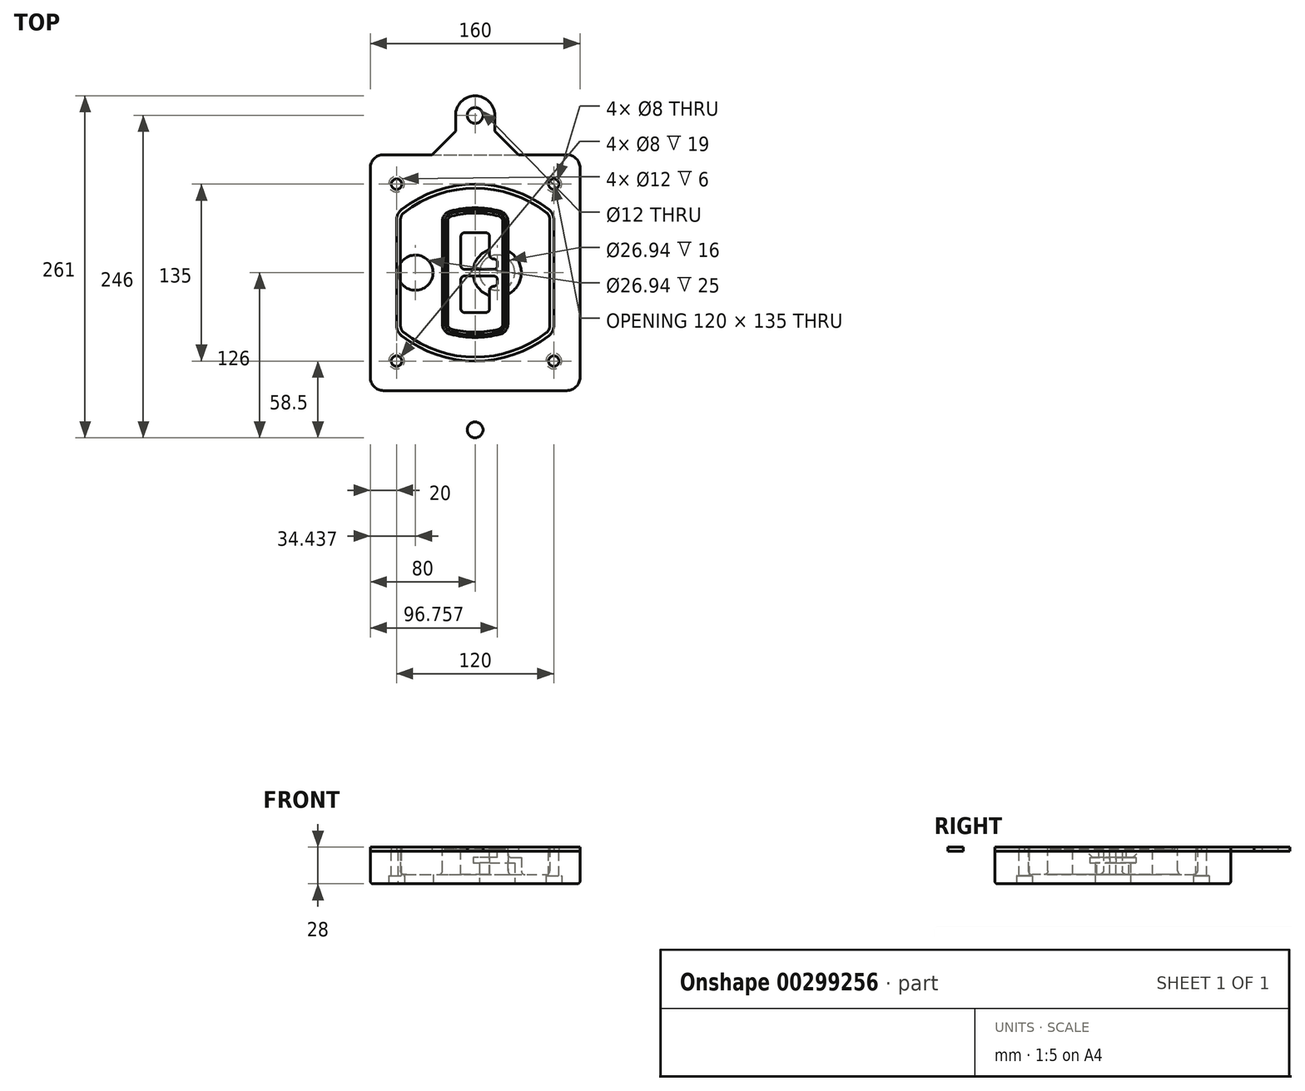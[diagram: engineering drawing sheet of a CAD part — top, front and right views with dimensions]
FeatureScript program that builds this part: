
annotation { "Feature Type Name" : "Feature", "Feature Type Description" : "" }
export const myFeature = defineFeature(function(context is Context, id is Id, definition is map)
    precondition{}
    {
        {
            var Q0;
            Q0=qCreatedBy(makeId("Top.planeOp"),FACE);
            var sketch = newSketch(context, id + "F0", { "sketchPlane" : qUnion([Q0])});
            skPoint(sketch, "E0.rect.middle", {"position": v(0, 0) * mm});
            skLineSegment(sketch, "E1.bottom", {"start": v(-70, -90) * mm, "end": v(70, -90) * mm});
            skLineSegment(sketch, "E1.top", {"start": v(-70, 90) * mm, "end": v(70, 90) * mm});
            skLineSegment(sketch, "E1.left", {"start": v(-80, -80) * mm, "end": v(-80, 80) * mm});
            skLineSegment(sketch, "E1.right", {"start": v(80, -80) * mm, "end": v(80, 80) * mm});
            skLineSegment(sketch, "E2", {"start": v(-80, 90) * mm, "end": v(80, -90) * mm, "construction": true});
            skLineSegment(sketch, "E3", {"start": v(80, 90) * mm, "end": v(-80, -90) * mm, "construction": true});
            skCircle(sketch, "E4", {"center": v(-60, 67.5) * mm, "radius": 4 * mm});
            skCircle(sketch, "E5", {"center": v(60, 67.5) * mm, "radius": 4 * mm});
            skCircle(sketch, "E6", {"center": v(60, -67.5) * mm, "radius": 4 * mm});
            skCircle(sketch, "E7", {"center": v(-60, -67.5) * mm, "radius": 4 * mm});
            skLineSegment(sketch, "E8", {"start": v(-60, 67.5) * mm, "end": v(60, 67.5) * mm, "construction": true});
            skLineSegment(sketch, "E9", {"start": v(60, 67.5) * mm, "end": v(60, -67.5) * mm, "construction": true});
            skLineSegment(sketch, "E10", {"start": v(60, -67.5) * mm, "end": v(-60, -67.5) * mm, "construction": true});
            skLineSegment(sketch, "E11", {"start": v(-60, -67.5) * mm, "end": v(-60, 67.5) * mm, "construction": true});
            skLineSegment(sketch, "E12", {"start": v(-60, 40.3) * mm, "end": v(-60, -40.3) * mm});
            skLineSegment(sketch, "E13", {"start": v(60, 40.3) * mm, "end": v(60, -40.3) * mm});
            skArc(sketch, "E14", {"start": v(56.15, 48.18) * mm, "mid": v(0, 67.5) * mm, "end": v(-56.15, 48.18) * mm});
            skArc(sketch, "E15", {"start": v(-56.15, -48.18) * mm, "mid": v(0, -67.5) * mm, "end": v(56.15, -48.18) * mm});
            skLineSegment(sketch, "E16", {"start": v(-60, 0) * mm, "end": v(60, 0) * mm, "construction": true});
            skPoint(sketch, "E17.visualSharp", {"position": v(-60, -45) * mm});
            skArc(sketch, "E17.filletArc", {"start": v(-60, -40.3) * mm, "mid": v(-58.99, -44.68) * mm, "end": v(-56.15, -48.18) * mm});
            skPoint(sketch, "E18.visualSharp", {"position": v(-60, 45) * mm});
            skArc(sketch, "E18.filletArc", {"start": v(-56.15, 48.18) * mm, "mid": v(-58.99, 44.68) * mm, "end": v(-60, 40.3) * mm});
            skPoint(sketch, "E19.visualSharp", {"position": v(60, 45) * mm});
            skArc(sketch, "E19.filletArc", {"start": v(60, 40.3) * mm, "mid": v(58.99, 44.68) * mm, "end": v(56.15, 48.18) * mm});
            skPoint(sketch, "E20.visualSharp", {"position": v(60, -45) * mm});
            skArc(sketch, "E20.filletArc", {"start": v(56.15, -48.18) * mm, "mid": v(58.99, -44.68) * mm, "end": v(60, -40.3) * mm});
            skPoint(sketch, "E21.visualSharp", {"position": v(-80, 90) * mm});
            skArc(sketch, "E21.filletArc", {"start": v(-70, 90) * mm, "mid": v(-77.07, 87.07) * mm, "end": v(-80, 80) * mm});
            skPoint(sketch, "E22.visualSharp", {"position": v(80, 90) * mm});
            skArc(sketch, "E22.filletArc", {"start": v(80, 80) * mm, "mid": v(77.07, 87.07) * mm, "end": v(70, 90) * mm});
            skPoint(sketch, "E23.visualSharp", {"position": v(80, -90) * mm});
            skArc(sketch, "E23.filletArc", {"start": v(70, -90) * mm, "mid": v(77.07, -87.07) * mm, "end": v(80, -80) * mm});
            skPoint(sketch, "E24.visualSharp", {"position": v(-80, -90) * mm});
            skArc(sketch, "E24.filletArc", {"start": v(-80, -80) * mm, "mid": v(-77.07, -87.07) * mm, "end": v(-70, -90) * mm});
            skArc(sketch, "E25.0", {"start": v(57, 40.3) * mm, "mid": v(56.3, 43.36) * mm, "end": v(54.3, 45.81) * mm});
            skLineSegment(sketch, "E25.1", {"start": v(57, 40.3) * mm, "end": v(57, -40.3) * mm});
            skArc(sketch, "E25.2", {"start": v(54.3, -45.81) * mm, "mid": v(56.3, -43.36) * mm, "end": v(57, -40.3) * mm});
            skArc(sketch, "E25.3", {"start": v(-54.3, -45.81) * mm, "mid": v(0, -64.5) * mm, "end": v(54.3, -45.81) * mm});
            skArc(sketch, "E25.4", {"start": v(-57, -40.3) * mm, "mid": v(-56.3, -43.36) * mm, "end": v(-54.3, -45.81) * mm});
            skArc(sketch, "E25.5", {"start": v(54.3, 45.81) * mm, "mid": v(0, 64.5) * mm, "end": v(-54.3, 45.81) * mm});
            skLineSegment(sketch, "E25.6", {"start": v(-57, 40.3) * mm, "end": v(-57, -40.3) * mm});
            skArc(sketch, "E25.7", {"start": v(-54.3, 45.81) * mm, "mid": v(-56.3, 43.36) * mm, "end": v(-57, 40.3) * mm});
            skArc(sketch, "E26.0", {"start": v(-58.62, 51.33) * mm, "mid": v(-62.58, 46.43) * mm, "end": v(-64, 40.3) * mm});
            skArc(sketch, "E26.1", {"start": v(58.62, 51.33) * mm, "mid": v(0, 71.5) * mm, "end": v(-58.62, 51.33) * mm});
            skArc(sketch, "E26.2", {"start": v(64, 40.3) * mm, "mid": v(62.58, 46.43) * mm, "end": v(58.62, 51.33) * mm});
            skLineSegment(sketch, "E26.3", {"start": v(64, 40.3) * mm, "end": v(64, -40.3) * mm});
            skArc(sketch, "E26.4", {"start": v(58.62, -51.33) * mm, "mid": v(62.58, -46.43) * mm, "end": v(64, -40.3) * mm});
            skLineSegment(sketch, "E26.5", {"start": v(-64, 40.3) * mm, "end": v(-64, -40.3) * mm});
            skArc(sketch, "E26.6", {"start": v(-58.62, -51.33) * mm, "mid": v(0, -71.5) * mm, "end": v(58.62, -51.33) * mm});
            skArc(sketch, "E26.7", {"start": v(-64, -40.3) * mm, "mid": v(-62.58, -46.43) * mm, "end": v(-58.62, -51.33) * mm});
            skSolve(sketch);
        }
        {
            var Q0;
            Q0=makeQuery(id+"F0.imprint","IMPRINT",FACE,{"disambiguationData":[TD([[makeQuery(id+"F0.imprint","IMPRINT",EDGE,{"derivedFrom":sQuery(id+"F0.wireOp",EDGE,"E1.bottom")}),1.0]])]});
            var Q1;
            Q1=makeQuery(id+"F0.imprint","IMPRINT",FACE,{"disambiguationData":[TD([[makeQuery(id+"F0.imprint","IMPRINT",EDGE,{"derivedFrom":sQuery(id+"F0.wireOp",EDGE,"E12")}),1.0]])]});
            var Q2;
            Q2=makeQuery(id+"F0.imprint","IMPRINT",FACE,{"disambiguationData":[TD([[makeQuery(id+"F0.imprint","IMPRINT",EDGE,{"derivedFrom":sQuery(id+"F0.wireOp",EDGE,"E25.0")}),1.0]])]});
            var Q3;
            Q3=makeQuery(id+"F0.imprint","IMPRINT",FACE,{"disambiguationData":[TD([[makeQuery(id+"F0.imprint","IMPRINT",EDGE,{"derivedFrom":sQuery(id+"F0.wireOp",EDGE,"E12")}),-1.0]])]});
            extrude(context, id + "F1", {"entities" : qUnion([Q0, Q1, Q2, Q3]), "oppositeDirection" : true, "depth" : 25 * mm});
        }
        {
            var Q0;
            Q0=makeQuery(id+"F0.imprint","IMPRINT",FACE,{"disambiguationData":[TD([[makeQuery(id+"F0.imprint","IMPRINT",EDGE,{"derivedFrom":sQuery(id+"F0.wireOp",EDGE,"E12")}),1.0]])]});
            extrude(context, id + "F2", {"entities" : qUnion([Q0]), "operationType" : NewBodyOperationType.ADD, "depth" : 3 * mm});
        }
        {
            var Q0;
            Q0=makeQuery(id+"F0.imprint","IMPRINT",FACE,{"disambiguationData":[TD([[makeQuery(id+"F0.imprint","IMPRINT",EDGE,{"derivedFrom":sQuery(id+"F0.wireOp",EDGE,"E25.0")}),1.0]])]});
            extrude(context, id + "F3", {"entities" : qUnion([Q0]), "operationType" : NewBodyOperationType.REMOVE, "oppositeDirection" : true, "depth" : 18 * mm});
        }
        {
            var Q0;
            Q0=makeQuery(id+"F2.opExtrude","CAP_FACE",FACE,{"disambiguationData":[OSD([sQuery(id+"F0.wireOp",EDGE,"E12"),sQuery(id+"F0.wireOp",EDGE,"E13"),sQuery(id+"F0.wireOp",EDGE,"E14"),sQuery(id+"F0.wireOp",EDGE,"E15"),sQuery(id+"F0.wireOp",EDGE,"E17.filletArc"),sQuery(id+"F0.wireOp",EDGE,"E18.filletArc"),sQuery(id+"F0.wireOp",EDGE,"E19.filletArc"),sQuery(id+"F0.wireOp",EDGE,"E20.filletArc"),sQuery(id+"F0.wireOp",EDGE,"E25.0"),sQuery(id+"F0.wireOp",EDGE,"E25.1"),sQuery(id+"F0.wireOp",EDGE,"E25.2"),sQuery(id+"F0.wireOp",EDGE,"E25.3"),sQuery(id+"F0.wireOp",EDGE,"E25.4"),sQuery(id+"F0.wireOp",EDGE,"E25.5"),sQuery(id+"F0.wireOp",EDGE,"E25.6"),sQuery(id+"F0.wireOp",EDGE,"E25.7")])],"isStart":false});
            var sketch = newSketch(context, id + "F4", { "sketchPlane" : qUnion([Q0])});
            skArc(sketch, "E27.0", {"start": v(-19.08, -46.97) * mm, "mid": v(0, -49.5) * mm, "end": v(19.08, -46.97) * mm});
            skArc(sketch, "E28.0", {"start": v(19.08, 46.97) * mm, "mid": v(0, 49.5) * mm, "end": v(-19.08, 46.97) * mm});
            skLineSegment(sketch, "E29", {"start": v(-25, 39.25) * mm, "end": v(-25, -39.25) * mm});
            skLineSegment(sketch, "E30", {"start": v(25, 39.25) * mm, "end": v(25, -39.25) * mm});
            skLineSegment(sketch, "E31", {"start": v(-25, 45.1) * mm, "end": v(25, 45.1) * mm, "construction": true});
            skLineSegment(sketch, "E32", {"start": v(-25, -45.1) * mm, "end": v(25, -45.1) * mm, "construction": true});
            skPoint(sketch, "E33.visualSharp", {"position": v(-25, 45.1) * mm});
            skArc(sketch, "E33.filletArc", {"start": v(-19.08, 46.97) * mm, "mid": v(-23.35, 44.11) * mm, "end": v(-25, 39.25) * mm});
            skPoint(sketch, "E34.visualSharp", {"position": v(25, 45.1) * mm});
            skArc(sketch, "E34.filletArc", {"start": v(25, 39.25) * mm, "mid": v(23.35, 44.11) * mm, "end": v(19.08, 46.97) * mm});
            skPoint(sketch, "E35.visualSharp", {"position": v(25, -45.1) * mm});
            skArc(sketch, "E35.filletArc", {"start": v(19.08, -46.97) * mm, "mid": v(23.35, -44.11) * mm, "end": v(25, -39.25) * mm});
            skPoint(sketch, "E36.visualSharp", {"position": v(-25, -45.1) * mm});
            skArc(sketch, "E36.filletArc", {"start": v(-25, -39.25) * mm, "mid": v(-23.35, -44.11) * mm, "end": v(-19.08, -46.97) * mm});
            skArc(sketch, "E37.0", {"start": v(54.3, 45.81) * mm, "mid": v(0, 64.5) * mm, "end": v(-54.3, 45.81) * mm});
            skArc(sketch, "E37.1", {"start": v(-54.3, 45.81) * mm, "mid": v(-56.3, 43.36) * mm, "end": v(-57, 40.3) * mm});
            skLineSegment(sketch, "E37.2", {"start": v(-57, 40.3) * mm, "end": v(-57, -40.3) * mm});
            skArc(sketch, "E37.3", {"start": v(-57, -40.3) * mm, "mid": v(-56.3, -43.36) * mm, "end": v(-54.3, -45.81) * mm});
            skArc(sketch, "E37.4", {"start": v(-54.3, -45.81) * mm, "mid": v(0, -64.5) * mm, "end": v(54.3, -45.81) * mm});
            skArc(sketch, "E37.5", {"start": v(54.3, -45.81) * mm, "mid": v(56.3, -43.36) * mm, "end": v(57, -40.3) * mm});
            skLineSegment(sketch, "E37.6", {"start": v(57, 40.3) * mm, "end": v(57, -40.3) * mm});
            skArc(sketch, "E37.7", {"start": v(57, 40.3) * mm, "mid": v(56.3, 43.36) * mm, "end": v(54.3, 45.81) * mm});
            skLineSegment(sketch, "E38.0", {"start": v(23, 39.25) * mm, "end": v(23, -39.25) * mm});
            skArc(sketch, "E38.1", {"start": v(18.56, -45.04) * mm, "mid": v(21.76, -42.9) * mm, "end": v(23, -39.25) * mm});
            skArc(sketch, "E38.2", {"start": v(-18.56, -45.04) * mm, "mid": v(0, -47.5) * mm, "end": v(18.56, -45.04) * mm});
            skArc(sketch, "E38.3", {"start": v(-23, -39.25) * mm, "mid": v(-21.76, -42.9) * mm, "end": v(-18.56, -45.04) * mm});
            skLineSegment(sketch, "E38.4", {"start": v(-23, 39.25) * mm, "end": v(-23, -39.25) * mm});
            skArc(sketch, "E38.5", {"start": v(23, 39.25) * mm, "mid": v(21.76, 42.9) * mm, "end": v(18.56, 45.04) * mm});
            skArc(sketch, "E38.6", {"start": v(-18.56, 45.04) * mm, "mid": v(-21.76, 42.9) * mm, "end": v(-23, 39.25) * mm});
            skArc(sketch, "E38.7", {"start": v(18.56, 45.04) * mm, "mid": v(0, 47.5) * mm, "end": v(-18.56, 45.04) * mm});
            skArc(sketch, "E39.0", {"start": v(21, 39.25) * mm, "mid": v(20.18, 41.68) * mm, "end": v(18.04, 43.1) * mm});
            skLineSegment(sketch, "E39.1", {"start": v(21, 39.25) * mm, "end": v(21, -39.25) * mm});
            skArc(sketch, "E39.2", {"start": v(18.04, -43.1) * mm, "mid": v(20.18, -41.68) * mm, "end": v(21, -39.25) * mm});
            skArc(sketch, "E39.3", {"start": v(-18.04, -43.1) * mm, "mid": v(0, -45.5) * mm, "end": v(18.04, -43.1) * mm});
            skArc(sketch, "E39.4", {"start": v(-21, -39.25) * mm, "mid": v(-20.18, -41.68) * mm, "end": v(-18.04, -43.1) * mm});
            skArc(sketch, "E39.5", {"start": v(18.04, 43.1) * mm, "mid": v(0, 45.5) * mm, "end": v(-18.04, 43.1) * mm});
            skLineSegment(sketch, "E39.6", {"start": v(-21, 39.25) * mm, "end": v(-21, -39.25) * mm});
            skArc(sketch, "E39.7", {"start": v(-18.04, 43.1) * mm, "mid": v(-20.18, 41.68) * mm, "end": v(-21, 39.25) * mm});
            skLineSegment(sketch, "E40", {"start": v(-25, 0) * mm, "end": v(25, 0) * mm, "construction": true});
            skLineSegment(sketch, "E41", {"start": v(-11, 5.5) * mm, "end": v(-11, 27.5) * mm});
            skLineSegment(sketch, "E42", {"start": v(-8, 30.5) * mm, "end": v(8, 30.5) * mm});
            skLineSegment(sketch, "E43", {"start": v(11, 27.5) * mm, "end": v(11, 13.5) * mm});
            skLineSegment(sketch, "E44", {"start": v(14, 10.5) * mm, "end": v(14, 10.5) * mm});
            skLineSegment(sketch, "E45", {"start": v(17, 7.5) * mm, "end": v(17, 5.5) * mm});
            skLineSegment(sketch, "E46", {"start": v(14, 2.5) * mm, "end": v(-8, 2.5) * mm});
            skPoint(sketch, "E47.visualSharp", {"position": v(-11, 30.5) * mm});
            skArc(sketch, "E47.filletArc", {"start": v(-8, 30.5) * mm, "mid": v(-10.12, 29.62) * mm, "end": v(-11, 27.5) * mm});
            skPoint(sketch, "E48.visualSharp", {"position": v(11, 30.5) * mm});
            skArc(sketch, "E48.filletArc", {"start": v(11, 27.5) * mm, "mid": v(10.12, 29.62) * mm, "end": v(8, 30.5) * mm});
            skPoint(sketch, "E49.visualSharp", {"position": v(11, 10.5) * mm});
            skArc(sketch, "E49.filletArc", {"start": v(11, 13.5) * mm, "mid": v(11.88, 11.38) * mm, "end": v(14, 10.5) * mm});
            skPoint(sketch, "E50.visualSharp", {"position": v(17, 10.5) * mm});
            skArc(sketch, "E50.filletArc", {"start": v(17, 7.5) * mm, "mid": v(16.12, 9.62) * mm, "end": v(14, 10.5) * mm});
            skPoint(sketch, "E51.visualSharp", {"position": v(17, 2.5) * mm});
            skArc(sketch, "E51.filletArc", {"start": v(14, 2.5) * mm, "mid": v(16.12, 3.38) * mm, "end": v(17, 5.5) * mm});
            skPoint(sketch, "E52.visualSharp", {"position": v(-11, 2.5) * mm});
            skArc(sketch, "E52.filletArc", {"start": v(-11, 5.5) * mm, "mid": v(-10.12, 3.38) * mm, "end": v(-8, 2.5) * mm});
            skLineSegment(sketch, "E53.0.MirrorCS", {"start": v(14, -2.5) * mm, "end": v(-8, -2.5) * mm});
            skArc(sketch, "E54.0.MirrorCS", {"start": v(-11, -5.5) * mm, "mid": v(-10.12, -3.38) * mm, "end": v(-8, -2.5) * mm});
            skLineSegment(sketch, "E55.0.MirrorCS", {"start": v(-11, -5.5) * mm, "end": v(-11, -27.5) * mm});
            skArc(sketch, "E56.0.MirrorCS", {"start": v(-8, -30.5) * mm, "mid": v(-10.12, -29.62) * mm, "end": v(-11, -27.5) * mm});
            skLineSegment(sketch, "E57.0.MirrorCS", {"start": v(-8, -30.5) * mm, "end": v(8, -30.5) * mm});
            skArc(sketch, "E58.0.MirrorCS", {"start": v(11, -27.5) * mm, "mid": v(10.12, -29.62) * mm, "end": v(8, -30.5) * mm});
            skLineSegment(sketch, "E59.0.MirrorCS", {"start": v(11, -27.5) * mm, "end": v(11, -13.5) * mm});
            skArc(sketch, "E60.0.MirrorCS", {"start": v(11, -13.5) * mm, "mid": v(11.88, -11.38) * mm, "end": v(14, -10.5) * mm});
            skArc(sketch, "E61.0.MirrorCS", {"start": v(17, -7.5) * mm, "mid": v(16.12, -9.62) * mm, "end": v(14, -10.5) * mm});
            skLineSegment(sketch, "E62.0.MirrorCS", {"start": v(17, -7.5) * mm, "end": v(17, -5.5) * mm});
            skArc(sketch, "E63.0.MirrorCS", {"start": v(14, -2.5) * mm, "mid": v(16.12, -3.38) * mm, "end": v(17, -5.5) * mm});
            skSolve(sketch);
        }
        {
            var Q0;
            Q0=makeQuery(id+"F4.imprint","IMPRINT",FACE,{"disambiguationData":[TD([[makeQuery(id+"F4.imprint","IMPRINT",EDGE,{"derivedFrom":sQuery(id+"F4.wireOp",EDGE,"E27.0")}),1.0]])]});
            var Q1;
            Q1=makeQuery(id+"F4.imprint","IMPRINT",FACE,{"disambiguationData":[TD([[makeQuery(id+"F4.imprint","IMPRINT",EDGE,{"derivedFrom":sQuery(id+"F4.wireOp",EDGE,"E38.0")}),-1.0]])]});
            var Q2;
            Q2=makeQuery(id+"F4.imprint","IMPRINT",FACE,{"disambiguationData":[TD([[makeQuery(id+"F4.imprint","IMPRINT",EDGE,{"derivedFrom":sQuery(id+"F4.wireOp",EDGE,"E39.0")}),1.0]])]});
            extrude(context, id + "F5", {"entities" : qUnion([Q0, Q1, Q2]), "operationType" : NewBodyOperationType.ADD, "endBound" : BoundingType.UP_TO_NEXT, "oppositeDirection" : true, "depth" : 25 * mm});
        }
        {
            var Q0;
            Q0=makeQuery(id+"F4.imprint","IMPRINT",FACE,{"disambiguationData":[TD([[makeQuery(id+"F4.imprint","IMPRINT",EDGE,{"derivedFrom":sQuery(id+"F4.wireOp",EDGE,"E38.0")}),-1.0]])]});
            extrude(context, id + "F6", {"entities" : qUnion([Q0]), "operationType" : NewBodyOperationType.REMOVE, "oppositeDirection" : true, "depth" : 2 * mm});
        }
        {
            var Q0;
            Q0=makeQuery(id+"F1.opExtrude","CAP_FACE",FACE,{"disambiguationData":[OSD([sQuery(id+"F0.wireOp",EDGE,"E1.bottom"),sQuery(id+"F0.wireOp",EDGE,"E1.top"),sQuery(id+"F0.wireOp",EDGE,"E1.left"),sQuery(id+"F0.wireOp",EDGE,"E1.right"),sQuery(id+"F0.wireOp",EDGE,"E4"),sQuery(id+"F0.wireOp",EDGE,"E5"),sQuery(id+"F0.wireOp",EDGE,"E6"),sQuery(id+"F0.wireOp",EDGE,"E7"),sQuery(id+"F0.wireOp",EDGE,"E21.filletArc"),sQuery(id+"F0.wireOp",EDGE,"E22.filletArc"),sQuery(id+"F0.wireOp",EDGE,"E23.filletArc"),sQuery(id+"F0.wireOp",EDGE,"E24.filletArc")])],"isStart":false});
            var sketch = newSketch(context, id + "F7", { "sketchPlane" : qUnion([Q0])});
            skCircle(sketch, "E64", {"center": v(16.76, 0) * mm, "radius": 13.47 * mm});
            skCircle(sketch, "E65", {"center": v(-45.56, 0) * mm, "radius": 13.47 * mm});
            skLineSegment(sketch, "E66", {"start": v(80, 0) * mm, "end": v(-80, 0) * mm});
            skCircle(sketch, "E67", {"center": v(16.76, 0) * mm, "radius": 18.47 * mm});
            skCircle(sketch, "E68", {"center": v(60, -67.5) * mm, "radius": 6 * mm});
            skCircle(sketch, "E69", {"center": v(-60, -67.5) * mm, "radius": 6 * mm});
            skCircle(sketch, "E70", {"center": v(-60, 67.5) * mm, "radius": 6 * mm});
            skCircle(sketch, "E71", {"center": v(60, 67.5) * mm, "radius": 6 * mm});
            skSolve(sketch);
        }
        {
            var Q0;
            {var subQ1=sQuery(id+"F7.wireOp",EDGE,"E66");var subQ4=sQuery(id+"F7.wireOp",EDGE,"E64");var subQ6=makeQuery(id+"F7.imprint","INTERSECT",VERTEX,{"disambiguationData":[OD(0.0)],"derivedFrom":[subQ4,subQ1]});Q0=makeQuery(id+"F7.imprint","IMPRINT",FACE,{"disambiguationData":[TD([[makeQuery(id+"F7.imprint","IMPRINT",EDGE,{"disambiguationData":[TD([[subQ6,-1.0]])],"derivedFrom":subQ4}),-1.0]])]});}
            var Q1;
            {var subQ0=sQuery(id+"F7.wireOp",EDGE,"E66");var subQ1=sQuery(id+"F7.wireOp",EDGE,"E64");var subQ3=makeQuery(id+"F7.imprint","INTERSECT",VERTEX,{"disambiguationData":[OD(0.0)],"derivedFrom":[subQ1,subQ0]});Q1=makeQuery(id+"F7.imprint","IMPRINT",FACE,{"disambiguationData":[TD([[makeQuery(id+"F7.imprint","IMPRINT",EDGE,{"disambiguationData":[TD([[subQ3,-1.0]])],"derivedFrom":subQ1}),1.0]])]});}
            var Q2;
            {var subQ0=sQuery(id+"F7.wireOp",EDGE,"E66");var subQ1=sQuery(id+"F7.wireOp",EDGE,"E64");var subQ3=makeQuery(id+"F7.imprint","INTERSECT",VERTEX,{"disambiguationData":[OD(0.0)],"derivedFrom":[subQ1,subQ0]});Q2=makeQuery(id+"F7.imprint","IMPRINT",FACE,{"disambiguationData":[TD([[makeQuery(id+"F7.imprint","IMPRINT",EDGE,{"disambiguationData":[TD([[subQ3,1.0]])],"derivedFrom":subQ1}),1.0]])]});}
            var Q3;
            {var subQ1=sQuery(id+"F7.wireOp",EDGE,"E66");var subQ4=sQuery(id+"F7.wireOp",EDGE,"E64");var subQ6=makeQuery(id+"F7.imprint","INTERSECT",VERTEX,{"disambiguationData":[OD(0.0)],"derivedFrom":[subQ4,subQ1]});Q3=makeQuery(id+"F7.imprint","IMPRINT",FACE,{"disambiguationData":[TD([[makeQuery(id+"F7.imprint","IMPRINT",EDGE,{"disambiguationData":[TD([[subQ6,1.0]])],"derivedFrom":subQ4}),-1.0]])]});}
            extrude(context, id + "F8", {"entities" : qUnion([Q0, Q1, Q2, Q3]), "operationType" : NewBodyOperationType.ADD, "oppositeDirection" : true, "depth" : 20 * mm});
        }
        {
            var Q0;
            {var subQ0=sQuery(id+"F7.wireOp",EDGE,"E66");var subQ1=sQuery(id+"F7.wireOp",EDGE,"E64");var subQ3=makeQuery(id+"F7.imprint","INTERSECT",VERTEX,{"disambiguationData":[OD(0.0)],"derivedFrom":[subQ1,subQ0]});Q0=makeQuery(id+"F7.imprint","IMPRINT",FACE,{"disambiguationData":[TD([[makeQuery(id+"F7.imprint","IMPRINT",EDGE,{"disambiguationData":[TD([[subQ3,-1.0]])],"derivedFrom":subQ1}),1.0]])]});}
            var Q1;
            {var subQ0=sQuery(id+"F7.wireOp",EDGE,"E66");var subQ1=sQuery(id+"F7.wireOp",EDGE,"E64");var subQ3=makeQuery(id+"F7.imprint","INTERSECT",VERTEX,{"disambiguationData":[OD(0.0)],"derivedFrom":[subQ1,subQ0]});Q1=makeQuery(id+"F7.imprint","IMPRINT",FACE,{"disambiguationData":[TD([[makeQuery(id+"F7.imprint","IMPRINT",EDGE,{"disambiguationData":[TD([[subQ3,1.0]])],"derivedFrom":subQ1}),1.0]])]});}
            extrude(context, id + "F9", {"entities" : qUnion([Q0, Q1]), "operationType" : NewBodyOperationType.REMOVE, "oppositeDirection" : true, "depth" : 16 * mm});
        }
        {
            var Q0;
            {var subQ0=sQuery(id+"F7.wireOp",EDGE,"E66");var subQ1=sQuery(id+"F7.wireOp",EDGE,"E65");var subQ3=makeQuery(id+"F7.imprint","INTERSECT",VERTEX,{"disambiguationData":[OD(0.0)],"derivedFrom":[subQ1,subQ0]});Q0=makeQuery(id+"F7.imprint","IMPRINT",FACE,{"disambiguationData":[TD([[makeQuery(id+"F7.imprint","IMPRINT",EDGE,{"disambiguationData":[TD([[subQ3,-1.0]])],"derivedFrom":subQ1}),1.0]])]});}
            var Q1;
            {var subQ0=sQuery(id+"F7.wireOp",EDGE,"E66");var subQ1=sQuery(id+"F7.wireOp",EDGE,"E65");var subQ3=makeQuery(id+"F7.imprint","INTERSECT",VERTEX,{"disambiguationData":[OD(0.0)],"derivedFrom":[subQ1,subQ0]});Q1=makeQuery(id+"F7.imprint","IMPRINT",FACE,{"disambiguationData":[TD([[makeQuery(id+"F7.imprint","IMPRINT",EDGE,{"disambiguationData":[TD([[subQ3,1.0]])],"derivedFrom":subQ1}),1.0]])]});}
            extrude(context, id + "F10", {"entities" : qUnion([Q0, Q1]), "operationType" : NewBodyOperationType.REMOVE, "oppositeDirection" : true, "depth" : 25 * mm});
        }
        {
            var Q0;
            Q0=makeQuery(id+"F7.imprint","IMPRINT",FACE,{"disambiguationData":[TD([[makeQuery(id+"F7.imprint","IMPRINT",EDGE,{"derivedFrom":sQuery(id+"F7.wireOp",EDGE,"E68")}),1.0]])]});
            var Q1;
            Q1=makeQuery(id+"F7.imprint","IMPRINT",FACE,{"disambiguationData":[TD([[makeQuery(id+"F7.imprint","IMPRINT",EDGE,{"derivedFrom":makeQuery(id+"F1.opExtrude","CAP_EDGE",EDGE,{"disambiguationData":[OSD([sQuery(id+"F0.wireOp",EDGE,"E5")])],"isStart":false})}),-1.0]])]});
            var Q2;
            Q2=makeQuery(id+"F7.imprint","IMPRINT",FACE,{"disambiguationData":[TD([[makeQuery(id+"F7.imprint","IMPRINT",EDGE,{"derivedFrom":sQuery(id+"F7.wireOp",EDGE,"E69")}),1.0]])]});
            var Q3;
            Q3=makeQuery(id+"F7.imprint","IMPRINT",FACE,{"disambiguationData":[TD([[makeQuery(id+"F7.imprint","IMPRINT",EDGE,{"derivedFrom":makeQuery(id+"F1.opExtrude","CAP_EDGE",EDGE,{"disambiguationData":[OSD([sQuery(id+"F0.wireOp",EDGE,"E4")])],"isStart":false})}),-1.0]])]});
            var Q4;
            Q4=makeQuery(id+"F7.imprint","IMPRINT",FACE,{"disambiguationData":[TD([[makeQuery(id+"F7.imprint","IMPRINT",EDGE,{"derivedFrom":sQuery(id+"F7.wireOp",EDGE,"E70")}),1.0]])]});
            var Q5;
            Q5=makeQuery(id+"F7.imprint","IMPRINT",FACE,{"disambiguationData":[TD([[makeQuery(id+"F7.imprint","IMPRINT",EDGE,{"derivedFrom":makeQuery(id+"F1.opExtrude","CAP_EDGE",EDGE,{"disambiguationData":[OSD([sQuery(id+"F0.wireOp",EDGE,"E7")])],"isStart":false})}),-1.0]])]});
            var Q6;
            Q6=makeQuery(id+"F7.imprint","IMPRINT",FACE,{"disambiguationData":[TD([[makeQuery(id+"F7.imprint","IMPRINT",EDGE,{"derivedFrom":sQuery(id+"F7.wireOp",EDGE,"E71")}),1.0]])]});
            var Q7;
            Q7=makeQuery(id+"F7.imprint","IMPRINT",FACE,{"disambiguationData":[TD([[makeQuery(id+"F7.imprint","IMPRINT",EDGE,{"derivedFrom":makeQuery(id+"F1.opExtrude","CAP_EDGE",EDGE,{"disambiguationData":[OSD([sQuery(id+"F0.wireOp",EDGE,"E6")])],"isStart":false})}),-1.0]])]});
            extrude(context, id + "F11", {"entities" : qUnion([Q0, Q1, Q2, Q3, Q4, Q5, Q6, Q7]), "operationType" : NewBodyOperationType.REMOVE, "oppositeDirection" : true, "depth" : 6 * mm});
        }
        {
            var Q0;
            Q0=makeQuery(id+"F9.boolean.opBoolean","COPY",FACE,{"derivedFrom":makeQuery(id+"F9.opExtrude","CAP_FACE",FACE,{"disambiguationData":[OSD([sQuery(id+"F7.wireOp",EDGE,"E64")])],"isStart":false})});
            var sketch = newSketch(context, id + "F12", { "sketchPlane" : qUnion([Q0])});
            skArc(sketch, "E72.0", {"start": v(11, 17.55) * mm, "mid": v(2.57, 11.82) * mm, "end": v(-1.54, 2.5) * mm});
            skArc(sketch, "E72.1", {"start": v(-1.54, -2.5) * mm, "mid": v(2.57, -11.82) * mm, "end": v(11, -17.55) * mm});
            skLineSegment(sketch, "E73", {"start": v(-1.54, -2.5) * mm, "end": v(14, -2.5) * mm});
            skLineSegment(sketch, "E74.0", {"start": v(14, 2.5) * mm, "end": v(-1.54, 2.5) * mm});
            skArc(sketch, "E74.1", {"start": v(14, 2.5) * mm, "mid": v(16.12, 3.38) * mm, "end": v(17, 5.5) * mm});
            skLineSegment(sketch, "E74.2", {"start": v(17, 7.5) * mm, "end": v(17, 5.5) * mm});
            skArc(sketch, "E74.3", {"start": v(17, 7.5) * mm, "mid": v(16.12, 9.62) * mm, "end": v(14, 10.5) * mm});
            skArc(sketch, "E74.4", {"start": v(11, 13.5) * mm, "mid": v(11.88, 11.38) * mm, "end": v(14, 10.5) * mm});
            skLineSegment(sketch, "E74.5", {"start": v(11, 17.55) * mm, "end": v(11, 13.5) * mm});
            skLineSegment(sketch, "E74.7", {"start": v(14, -2.5) * mm, "end": v(-1.54, -2.5) * mm});
            skArc(sketch, "E74.8", {"start": v(14, -2.5) * mm, "mid": v(16.12, -3.38) * mm, "end": v(17, -5.5) * mm});
            skLineSegment(sketch, "E74.9", {"start": v(17, -7.5) * mm, "end": v(17, -5.5) * mm});
            skArc(sketch, "E74.10", {"start": v(17, -7.5) * mm, "mid": v(16.12, -9.62) * mm, "end": v(14, -10.5) * mm});
            skArc(sketch, "E74.11", {"start": v(11, -13.5) * mm, "mid": v(11.88, -11.38) * mm, "end": v(14, -10.5) * mm});
            skLineSegment(sketch, "E74.12", {"start": v(11, -17.55) * mm, "end": v(11, -13.5) * mm});
            skPoint(sketch, "E75.orphan", {"position": v(11, -27.5) * mm});
            skPoint(sketch, "E76.orphan", {"position": v(-8, -2.5) * mm});
            skPoint(sketch, "E77.orphan", {"position": v(-8, 2.5) * mm});
            skPoint(sketch, "E78.orphan", {"position": v(11, 27.5) * mm});
            skSolve(sketch);
        }
        {
            var Q0;
            {var subQ7=sQuery(id+"F12.wireOp",EDGE,"E72.0");var subQ14=sQuery(id+"F12.wireOp",EDGE,"E72.1");var subQ16=sQuery(id+"F12.wireOp",EDGE,"E74.1");var subQ18=sQuery(id+"F12.wireOp",EDGE,"E74.8");Q0=qUnion([makeQuery(id+"F12.imprint","IMPRINT",FACE,{"disambiguationData":[TD([[makeQuery(id+"F12.imprint","IMPRINT",EDGE,{"derivedFrom":subQ7}),1.0]])]}),makeQuery(id+"F12.imprint","IMPRINT",FACE,{"disambiguationData":[TD([[makeQuery(id+"F12.imprint","IMPRINT",EDGE,{"derivedFrom":subQ14}),1.0]])]}),makeQuery(id+"F12.imprint","IMPRINT",FACE,{"disambiguationData":[TD([[makeQuery(id+"F12.imprint","IMPRINT",EDGE,{"derivedFrom":subQ16}),1.0]])]}),makeQuery(id+"F12.imprint","IMPRINT",FACE,{"disambiguationData":[TD([[makeQuery(id+"F12.imprint","IMPRINT",EDGE,{"derivedFrom":subQ18}),-1.0]])]})]);}
            var Q1;
            Q1=makeQuery(id+"F5.boolean.opBoolean","SPLIT",FACE,{"disambiguationData":[TD([makeQuery(id+"F5.opExtrude","SWEPT_FACE",FACE,{"disambiguationData":[OSD([sQuery(id+"F4.wireOp",EDGE,"E41")])]})])],"derivedFrom":makeQuery(id+"F3.boolean.opBoolean","COPY",FACE,{"derivedFrom":makeQuery(id+"F3.opExtrude","CAP_FACE",FACE,{"disambiguationData":[OSD([sQuery(id+"F0.wireOp",EDGE,"E25.0"),sQuery(id+"F0.wireOp",EDGE,"E25.1"),sQuery(id+"F0.wireOp",EDGE,"E25.2"),sQuery(id+"F0.wireOp",EDGE,"E25.3"),sQuery(id+"F0.wireOp",EDGE,"E25.4"),sQuery(id+"F0.wireOp",EDGE,"E25.5"),sQuery(id+"F0.wireOp",EDGE,"E25.6"),sQuery(id+"F0.wireOp",EDGE,"E25.7")])],"isStart":false})})});
            extrude(context, id + "F13", {"entities" : qUnion([Q0]), "operationType" : NewBodyOperationType.REMOVE, "endBound" : BoundingType.UP_TO_SURFACE, "endBoundEntityFace" : qUnion([Q1]), "depth" : 25 * mm});
        }
        {
            var Q0;
            Q0=makeQuery(id+"F3.boolean.opBoolean","COPY",EDGE,{"derivedFrom":makeQuery(id+"F3.opExtrude","CAP_EDGE",EDGE,{"disambiguationData":[OSD([sQuery(id+"F0.wireOp",EDGE,"E25.6")])],"isStart":false})});
            var Q1;
            Q1=makeQuery(id+"F8.boolean.opBoolean","INTERSECT",EDGE,{"derivedFrom":[makeQuery(id+"F5.opExtrude","SWEPT_FACE",FACE,{"disambiguationData":[OSD([sQuery(id+"F4.wireOp",EDGE,"E30")])]}),makeQuery(id+"F8.opExtrude","CAP_FACE",FACE,{"disambiguationData":[OSD([sQuery(id+"F7.wireOp",EDGE,"E67")])],"isStart":false})]});
            var Q2;
            Q2=makeQuery(id+"F8.boolean.opBoolean","INTERSECT",EDGE,{"disambiguationData":[OD(1.0)],"derivedFrom":[makeQuery(id+"F5.opExtrude","SWEPT_FACE",FACE,{"disambiguationData":[OSD([sQuery(id+"F4.wireOp",EDGE,"E30")])]}),makeQuery(id+"F8.opExtrude","SWEPT_FACE",FACE,{"disambiguationData":[OSD([sQuery(id+"F7.wireOp",EDGE,"E67")])]})]});
            var Q3;
            {var subQ0=sQuery(id+"F4.wireOp",EDGE,"E30");Q3=makeQuery(id+"F8.boolean.opBoolean","SPLIT",EDGE,{"disambiguationData":[TD([makeQuery(id+"F5.opExtrude","SWEPT_FACE",FACE,{"disambiguationData":[OSD([sQuery(id+"F4.wireOp",EDGE,"E35.filletArc")])]})])],"derivedFrom":makeQuery(id+"F5.opExtrude","CAP_EDGE",EDGE,{"disambiguationData":[OSD([subQ0])],"isStart":false})});}
            var Q4;
            {var subQ0=sQuery(id+"F0.wireOp",EDGE,"E25.7");var subQ1=sQuery(id+"F0.wireOp",EDGE,"E25.1");var subQ2=sQuery(id+"F0.wireOp",EDGE,"E25.6");var subQ3=sQuery(id+"F0.wireOp",EDGE,"E25.5");var subQ4=sQuery(id+"F0.wireOp",EDGE,"E25.4");var subQ5=sQuery(id+"F0.wireOp",EDGE,"E25.0");var subQ6=sQuery(id+"F0.wireOp",EDGE,"E25.2");var subQ7=sQuery(id+"F0.wireOp",EDGE,"E25.3");Q4=makeQuery(id+"F8.boolean.opBoolean","INTERSECT",EDGE,{"derivedFrom":[makeQuery(id+"F5.boolean.opBoolean","SPLIT",FACE,{"disambiguationData":[TD([makeQuery(id+"F2.opExtrude","SWEPT_FACE",FACE,{"disambiguationData":[OSD([subQ5])]})])],"derivedFrom":makeQuery(id+"F3.boolean.opBoolean","COPY",FACE,{"derivedFrom":makeQuery(id+"F3.opExtrude","CAP_FACE",FACE,{"disambiguationData":[OSD([subQ5,subQ1,subQ6,subQ7,subQ4,subQ3,subQ2,subQ0])],"isStart":false})})}),makeQuery(id+"F8.opExtrude","SWEPT_FACE",FACE,{"disambiguationData":[OSD([sQuery(id+"F7.wireOp",EDGE,"E67")])]})]});}
            var Q5;
            Q5=makeQuery(id+"F8.boolean.opBoolean","INTERSECT",EDGE,{"disambiguationData":[OD(0.0)],"derivedFrom":[makeQuery(id+"F5.opExtrude","SWEPT_FACE",FACE,{"disambiguationData":[OSD([sQuery(id+"F4.wireOp",EDGE,"E30")])]}),makeQuery(id+"F8.opExtrude","SWEPT_FACE",FACE,{"disambiguationData":[OSD([sQuery(id+"F7.wireOp",EDGE,"E67")])]})]});
            fillet(context, id + "F14", {"entities" : qUnion([Q0, Q1, Q2, Q3, Q4, Q5]), "radius" : 3 * mm, "tangentPropagation" : true, "allowEdgeOverflow" : false});
        }
        {
            var Q0;
            Q0=makeQuery(id+"F1.opExtrude","CAP_EDGE",EDGE,{"disambiguationData":[OSD([sQuery(id+"F0.wireOp",EDGE,"E1.bottom")])],"isStart":false});
            fillet(context, id + "F15", {"entities" : qUnion([Q0]), "radius" : 2 * mm, "tangentPropagation" : true, "allowEdgeOverflow" : false});
        }
        {
            var Q0;
            {var subQ0=sQuery(id+"F0.wireOp",EDGE,"E21.filletArc");var subQ1=sQuery(id+"F0.wireOp",EDGE,"E7");var subQ2=sQuery(id+"F0.wireOp",EDGE,"E6");var subQ3=sQuery(id+"F0.wireOp",EDGE,"E5");var subQ4=sQuery(id+"F0.wireOp",EDGE,"E4");var subQ5=sQuery(id+"F0.wireOp",EDGE,"E22.filletArc");var subQ6=sQuery(id+"F0.wireOp",EDGE,"E1.bottom");var subQ7=sQuery(id+"F0.wireOp",EDGE,"E1.right");var subQ8=sQuery(id+"F0.wireOp",EDGE,"E1.top");var subQ9=sQuery(id+"F0.wireOp",EDGE,"E1.left");var subQ10=sQuery(id+"F0.wireOp",EDGE,"E23.filletArc");var subQ11=sQuery(id+"F0.wireOp",EDGE,"E24.filletArc");Q0=makeQuery(id+"F2.boolean.opBoolean","SPLIT",FACE,{"disambiguationData":[TD([makeQuery(id+"F1.opExtrude","SWEPT_FACE",FACE,{"disambiguationData":[OSD([subQ6])]})])],"derivedFrom":makeQuery(id+"F1.opExtrude","CAP_FACE",FACE,{"disambiguationData":[OSD([subQ6,subQ8,subQ9,subQ7,subQ4,subQ3,subQ2,subQ1,subQ0,subQ5,subQ10,subQ11])],"isStart":true})});}
            var sketch = newSketch(context, id + "F16", { "sketchPlane" : qUnion([Q0])});
            skPoint(sketch, "E79.startSnap0", {"position": v(0, 90) * mm});
            skLineSegment(sketch, "E80", {"start": v(0, 90) * mm, "end": v(0, 120) * mm, "construction": true});
            skCircle(sketch, "E81", {"center": v(0, 120) * mm, "radius": 6 * mm});
            skArc(sketch, "E82", {"start": v(15, 120) * mm, "mid": v(0, 135) * mm, "end": v(-15, 120) * mm});
            skLineSegment(sketch, "E83", {"start": v(15, 120) * mm, "end": v(15, 108) * mm});
            skLineSegment(sketch, "E84", {"start": v(-15, 120) * mm, "end": v(-15, 108) * mm});
            skLineSegment(sketch, "E85", {"start": v(-15, 108) * mm, "end": v(-33, 90) * mm});
            skLineSegment(sketch, "E86", {"start": v(15, 108) * mm, "end": v(33, 90) * mm});
            skLineSegment(sketch, "E87", {"start": v(-80, 0) * mm, "end": v(80, 0) * mm, "construction": true});
            skCircle(sketch, "E88.MirrorC", {"center": v(0, -120) * mm, "radius": 6 * mm});
            skArc(sketch, "E89.MirrorCS", {"start": v(15, -120) * mm, "mid": v(0, -135) * mm, "end": v(-15, -120) * mm});
            skPoint(sketch, "E90.MirrorP", {"position": v(0, -90) * mm});
            skLineSegment(sketch, "E91.MirrorCS", {"start": v(0, -90) * mm, "end": v(0, -120) * mm, "construction": true});
            skLineSegment(sketch, "E92.MirrorCS", {"start": v(15, -120) * mm, "end": v(15, -108) * mm});
            skLineSegment(sketch, "E93.MirrorCS", {"start": v(-15, -120) * mm, "end": v(-15, -108) * mm});
            skLineSegment(sketch, "E94.MirrorCS", {"start": v(-15, -108) * mm, "end": v(-33, -90) * mm});
            skLineSegment(sketch, "E95.MirrorCS", {"start": v(15, -108) * mm, "end": v(33, -90) * mm});
            skArc(sketch, "E96.MirrorCS", {"start": v(-15, 120) * mm, "mid": v(0, 135) * mm, "end": v(15, 120) * mm});
            skSolve(sketch);
        }
        {
            var Q0;
            Q0=makeQuery(id+"F16.imprint","IMPRINT",FACE,{"disambiguationData":[TD([[makeQuery(id+"F16.imprint","IMPRINT",EDGE,{"derivedFrom":makeQuery(id+"F1.opExtrude","CAP_EDGE",EDGE,{"disambiguationData":[OSD([sQuery(id+"F0.wireOp",EDGE,"E1.left")])],"isStart":true})}),-1.0]])]});
            var Q1;
            {var subQ1=sQuery(id+"F16.wireOp",EDGE,"E86");Q1=makeQuery(id+"F16.imprint","IMPRINT",FACE,{"disambiguationData":[TD([[makeQuery(id+"F16.imprint","IMPRINT",EDGE,{"derivedFrom":subQ1}),-1.0]])]});}
            var Q2;
            Q2=makeQuery(id+"F16.imprint","IMPRINT",FACE,{"disambiguationData":[TD([[makeQuery(id+"F16.imprint","IMPRINT",EDGE,{"derivedFrom":sQuery(id+"F16.wireOp",EDGE,"E88.MirrorC")}),1.0]])]});
            var Q3;
            Q3=makeQuery(id+"F2.opExtrude","CAP_FACE",FACE,{"disambiguationData":[OSD([sQuery(id+"F0.wireOp",EDGE,"E12"),sQuery(id+"F0.wireOp",EDGE,"E13"),sQuery(id+"F0.wireOp",EDGE,"E14"),sQuery(id+"F0.wireOp",EDGE,"E15"),sQuery(id+"F0.wireOp",EDGE,"E17.filletArc"),sQuery(id+"F0.wireOp",EDGE,"E18.filletArc"),sQuery(id+"F0.wireOp",EDGE,"E19.filletArc"),sQuery(id+"F0.wireOp",EDGE,"E20.filletArc"),sQuery(id+"F0.wireOp",EDGE,"E25.0"),sQuery(id+"F0.wireOp",EDGE,"E25.1"),sQuery(id+"F0.wireOp",EDGE,"E25.2"),sQuery(id+"F0.wireOp",EDGE,"E25.3"),sQuery(id+"F0.wireOp",EDGE,"E25.4"),sQuery(id+"F0.wireOp",EDGE,"E25.5"),sQuery(id+"F0.wireOp",EDGE,"E25.6"),sQuery(id+"F0.wireOp",EDGE,"E25.7")])],"isStart":false});
            extrude(context, id + "F17", {"entities" : qUnion([Q0, Q1, Q2]), "endBound" : BoundingType.UP_TO_SURFACE, "endBoundEntityFace" : qUnion([Q3]), "depth" : 25 * mm});
        }
    });
